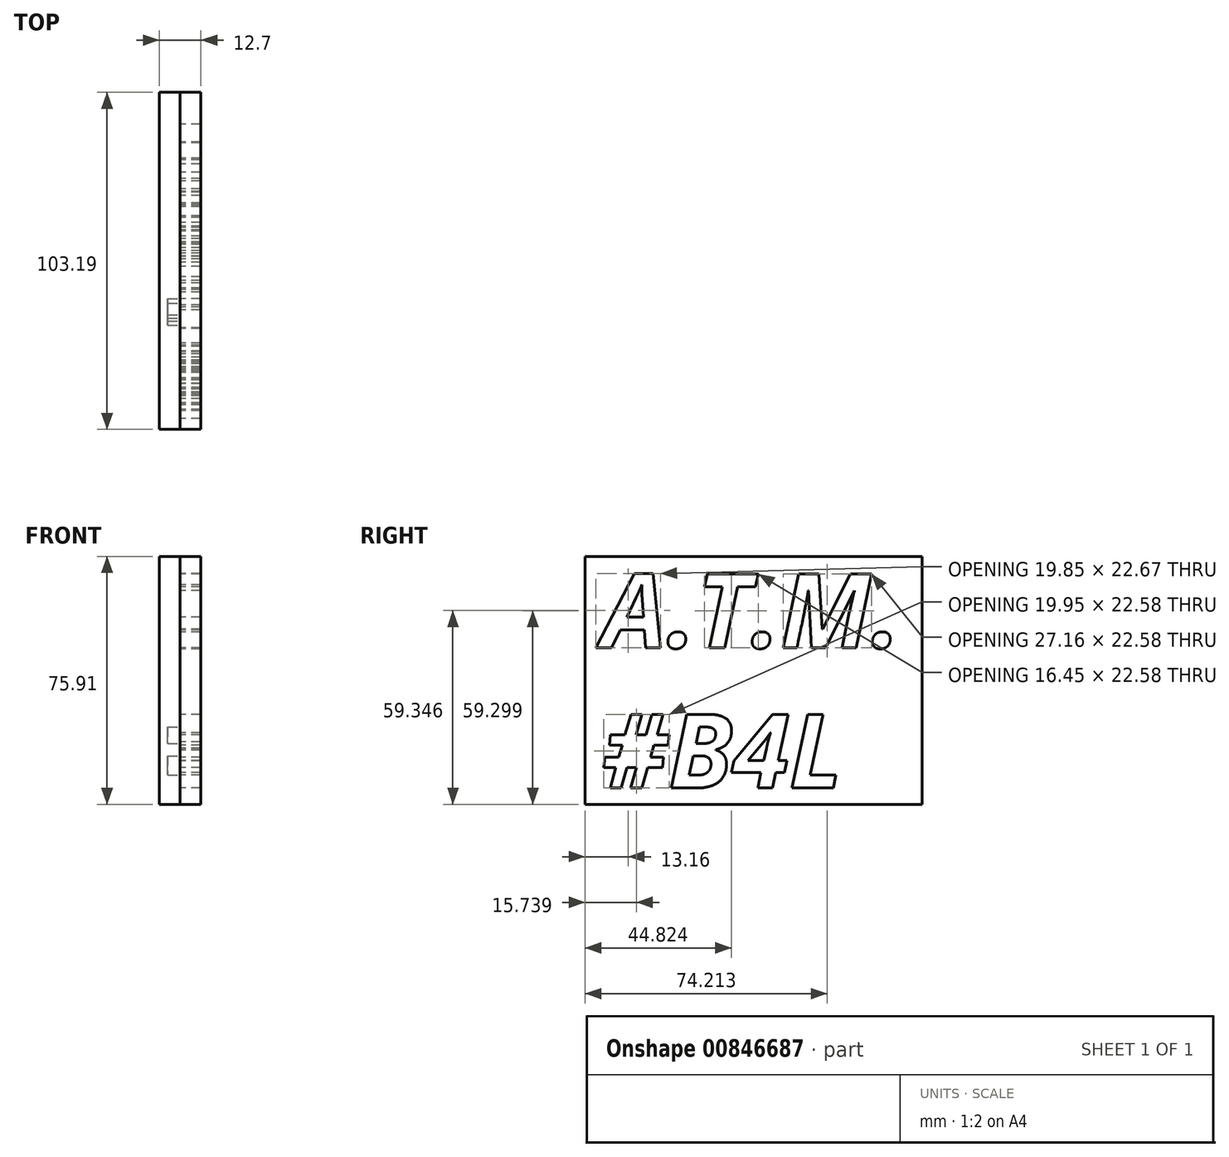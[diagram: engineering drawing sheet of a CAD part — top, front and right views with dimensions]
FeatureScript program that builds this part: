
annotation { "Feature Type Name" : "Feature", "Feature Type Description" : "" }
export const myFeature = defineFeature(function(context is Context, id is Id, definition is map)
    precondition{}
    {
        {
            var Q0;
            Q0=qCreatedBy(makeId("Right.planeOp"),FACE);
            var sketch = newSketch(context, id + "F0", { "sketchPlane" : qUnion([Q0])});
            skLineSegment(sketch, "E0.bottom", {"start": v(-51.7, 33.34) * mm, "end": v(51.5, 33.34) * mm});
            skLineSegment(sketch, "E0.top", {"start": v(-51.7, -42.57) * mm, "end": v(51.5, -42.57) * mm});
            skLineSegment(sketch, "E0.left", {"start": v(-51.7, 33.34) * mm, "end": v(-51.7, -42.57) * mm});
            skLineSegment(sketch, "E0.right", {"start": v(51.5, 33.34) * mm, "end": v(51.5, -42.57) * mm});
            skText(sketch, "E1", { "text": "A.T.M.\n#B4L\n", "fontName": "OpenSans-BoldItalic.ttf"});
            const initialGuessF0  = {"E1": [-0.04657, 0.00544, 1, 0, 0.02277]};
            skSetInitialGuess(sketch, initialGuessF0);
            skSolve(sketch);
        }
        {
            var Q0;
            Q0 = qSketchRegion(id + "F0", true);
            var Q1;
            Q1=makeQuery(id+"F0.imprint","IMPRINT",FACE,{"disambiguationData":[TD([[makeQuery(id+"F0.imprint","IMPRINT",EDGE,{"derivedFrom":sQuery(id+"F0.wireOp",EDGE,"E1.sketch_text.stroke-8")}),1.0]])]});
            var Q2;
            Q2=makeQuery(id+"F0.imprint","IMPRINT",FACE,{"disambiguationData":[TD([[makeQuery(id+"F0.imprint","IMPRINT",EDGE,{"derivedFrom":sQuery(id+"F0.wireOp",EDGE,"E1.sketch_text.stroke-131")}),1.0]])]});
            extrude(context, id + "F1", {"entities" : qUnion([Q0, Q1, Q2]), "depth" : 6.35 * mm, "offsetDistance" : 25.4 * mm});
        }
        {
            var Q0;
            Q0=makeQuery(id+"F0.imprint","IMPRINT",FACE,{"disambiguationData":[TD([[makeQuery(id+"F0.imprint","IMPRINT",EDGE,{"derivedFrom":sQuery(id+"F0.wireOp",EDGE,"E1.sketch_text.stroke-108")}),1.0]])]});
            var Q1;
            Q1=makeQuery(id+"F0.imprint","IMPRINT",FACE,{"disambiguationData":[TD([[makeQuery(id+"F0.imprint","IMPRINT",EDGE,{"derivedFrom":sQuery(id+"F0.wireOp",EDGE,"E1.sketch_text.stroke-114")}),1.0]])]});
            extrude(context, id + "F2", {"entities" : qUnion([Q0, Q1]), "operationType" : NewBodyOperationType.ADD, "oppositeDirection" : true, "depth" : 3.8 * mm, "offsetDistance" : 25.4 * mm});
        }
        {
            var Q0;
            Q0=makeQuery(id+"F1.opExtrude","CAP_FACE",FACE,{"disambiguationData":[OSD([sQuery(id+"F0.wireOp",EDGE,"E0.bottom"),sQuery(id+"F0.wireOp",EDGE,"E0.top"),sQuery(id+"F0.wireOp",EDGE,"E0.left"),sQuery(id+"F0.wireOp",EDGE,"E0.right"),sQuery(id+"F0.wireOp",EDGE,"E1.sketch_text.stroke-0"),sQuery(id+"F0.wireOp",EDGE,"E1.sketch_text.stroke-1"),sQuery(id+"F0.wireOp",EDGE,"E1.sketch_text.stroke-2"),sQuery(id+"F0.wireOp",EDGE,"E1.sketch_text.stroke-3"),sQuery(id+"F0.wireOp",EDGE,"E1.sketch_text.stroke-4"),sQuery(id+"F0.wireOp",EDGE,"E1.sketch_text.stroke-5"),sQuery(id+"F0.wireOp",EDGE,"E1.sketch_text.stroke-6"),sQuery(id+"F0.wireOp",EDGE,"E1.sketch_text.stroke-7"),sQuery(id+"F0.wireOp",EDGE,"E1.sketch_text.stroke-14"),sQuery(id+"F0.wireOp",EDGE,"E1.sketch_text.stroke-15"),sQuery(id+"F0.wireOp",EDGE,"E1.sketch_text.stroke-16"),sQuery(id+"F0.wireOp",EDGE,"E1.sketch_text.stroke-17"),sQuery(id+"F0.wireOp",EDGE,"E1.sketch_text.stroke-18"),sQuery(id+"F0.wireOp",EDGE,"E1.sketch_text.stroke-19"),sQuery(id+"F0.wireOp",EDGE,"E1.sketch_text.stroke-20"),sQuery(id+"F0.wireOp",EDGE,"E1.sketch_text.stroke-21"),sQuery(id+"F0.wireOp",EDGE,"E1.sketch_text.stroke-22"),sQuery(id+"F0.wireOp",EDGE,"E1.sketch_text.stroke-23"),sQuery(id+"F0.wireOp",EDGE,"E1.sketch_text.stroke-24"),sQuery(id+"F0.wireOp",EDGE,"E1.sketch_text.stroke-25"),sQuery(id+"F0.wireOp",EDGE,"E1.sketch_text.stroke-26"),sQuery(id+"F0.wireOp",EDGE,"E1.sketch_text.stroke-27"),sQuery(id+"F0.wireOp",EDGE,"E1.sketch_text.stroke-28"),sQuery(id+"F0.wireOp",EDGE,"E1.sketch_text.stroke-29"),sQuery(id+"F0.wireOp",EDGE,"E1.sketch_text.stroke-30"),sQuery(id+"F0.wireOp",EDGE,"E1.sketch_text.stroke-31"),sQuery(id+"F0.wireOp",EDGE,"E1.sketch_text.stroke-32"),sQuery(id+"F0.wireOp",EDGE,"E1.sketch_text.stroke-33"),sQuery(id+"F0.wireOp",EDGE,"E1.sketch_text.stroke-34"),sQuery(id+"F0.wireOp",EDGE,"E1.sketch_text.stroke-35"),sQuery(id+"F0.wireOp",EDGE,"E1.sketch_text.stroke-36"),sQuery(id+"F0.wireOp",EDGE,"E1.sketch_text.stroke-37"),sQuery(id+"F0.wireOp",EDGE,"E1.sketch_text.stroke-38"),sQuery(id+"F0.wireOp",EDGE,"E1.sketch_text.stroke-39"),sQuery(id+"F0.wireOp",EDGE,"E1.sketch_text.stroke-40"),sQuery(id+"F0.wireOp",EDGE,"E1.sketch_text.stroke-41"),sQuery(id+"F0.wireOp",EDGE,"E1.sketch_text.stroke-42"),sQuery(id+"F0.wireOp",EDGE,"E1.sketch_text.stroke-43"),sQuery(id+"F0.wireOp",EDGE,"E1.sketch_text.stroke-44"),sQuery(id+"F0.wireOp",EDGE,"E1.sketch_text.stroke-45"),sQuery(id+"F0.wireOp",EDGE,"E1.sketch_text.stroke-46"),sQuery(id+"F0.wireOp",EDGE,"E1.sketch_text.stroke-47"),sQuery(id+"F0.wireOp",EDGE,"E1.sketch_text.stroke-48"),sQuery(id+"F0.wireOp",EDGE,"E1.sketch_text.stroke-49"),sQuery(id+"F0.wireOp",EDGE,"E1.sketch_text.stroke-50"),sQuery(id+"F0.wireOp",EDGE,"E1.sketch_text.stroke-51"),sQuery(id+"F0.wireOp",EDGE,"E1.sketch_text.stroke-52"),sQuery(id+"F0.wireOp",EDGE,"E1.sketch_text.stroke-53"),sQuery(id+"F0.wireOp",EDGE,"E1.sketch_text.stroke-54"),sQuery(id+"F0.wireOp",EDGE,"E1.sketch_text.stroke-55"),sQuery(id+"F0.wireOp",EDGE,"E1.sketch_text.stroke-56"),sQuery(id+"F0.wireOp",EDGE,"E1.sketch_text.stroke-57"),sQuery(id+"F0.wireOp",EDGE,"E1.sketch_text.stroke-58"),sQuery(id+"F0.wireOp",EDGE,"E1.sketch_text.stroke-59"),sQuery(id+"F0.wireOp",EDGE,"E1.sketch_text.stroke-60"),sQuery(id+"F0.wireOp",EDGE,"E1.sketch_text.stroke-61"),sQuery(id+"F0.wireOp",EDGE,"E1.sketch_text.stroke-62"),sQuery(id+"F0.wireOp",EDGE,"E1.sketch_text.stroke-63"),sQuery(id+"F0.wireOp",EDGE,"E1.sketch_text.stroke-64"),sQuery(id+"F0.wireOp",EDGE,"E1.sketch_text.stroke-65"),sQuery(id+"F0.wireOp",EDGE,"E1.sketch_text.stroke-66"),sQuery(id+"F0.wireOp",EDGE,"E1.sketch_text.stroke-67"),sQuery(id+"F0.wireOp",EDGE,"E1.sketch_text.stroke-68"),sQuery(id+"F0.wireOp",EDGE,"E1.sketch_text.stroke-69"),sQuery(id+"F0.wireOp",EDGE,"E1.sketch_text.stroke-70"),sQuery(id+"F0.wireOp",EDGE,"E1.sketch_text.stroke-71"),sQuery(id+"F0.wireOp",EDGE,"E1.sketch_text.stroke-72"),sQuery(id+"F0.wireOp",EDGE,"E1.sketch_text.stroke-73"),sQuery(id+"F0.wireOp",EDGE,"E1.sketch_text.stroke-74"),sQuery(id+"F0.wireOp",EDGE,"E1.sketch_text.stroke-75"),sQuery(id+"F0.wireOp",EDGE,"E1.sketch_text.stroke-76"),sQuery(id+"F0.wireOp",EDGE,"E1.sketch_text.stroke-77"),sQuery(id+"F0.wireOp",EDGE,"E1.sketch_text.stroke-78"),sQuery(id+"F0.wireOp",EDGE,"E1.sketch_text.stroke-79"),sQuery(id+"F0.wireOp",EDGE,"E1.sketch_text.stroke-80"),sQuery(id+"F0.wireOp",EDGE,"E1.sketch_text.stroke-81"),sQuery(id+"F0.wireOp",EDGE,"E1.sketch_text.stroke-82"),sQuery(id+"F0.wireOp",EDGE,"E1.sketch_text.stroke-83"),sQuery(id+"F0.wireOp",EDGE,"E1.sketch_text.stroke-84"),sQuery(id+"F0.wireOp",EDGE,"E1.sketch_text.stroke-85"),sQuery(id+"F0.wireOp",EDGE,"E1.sketch_text.stroke-86"),sQuery(id+"F0.wireOp",EDGE,"E1.sketch_text.stroke-87"),sQuery(id+"F0.wireOp",EDGE,"E1.sketch_text.stroke-88"),sQuery(id+"F0.wireOp",EDGE,"E1.sketch_text.stroke-89"),sQuery(id+"F0.wireOp",EDGE,"E1.sketch_text.stroke-90"),sQuery(id+"F0.wireOp",EDGE,"E1.sketch_text.stroke-91"),sQuery(id+"F0.wireOp",EDGE,"E1.sketch_text.stroke-96"),sQuery(id+"F0.wireOp",EDGE,"E1.sketch_text.stroke-97"),sQuery(id+"F0.wireOp",EDGE,"E1.sketch_text.stroke-98"),sQuery(id+"F0.wireOp",EDGE,"E1.sketch_text.stroke-99"),sQuery(id+"F0.wireOp",EDGE,"E1.sketch_text.stroke-100"),sQuery(id+"F0.wireOp",EDGE,"E1.sketch_text.stroke-101"),sQuery(id+"F0.wireOp",EDGE,"E1.sketch_text.stroke-102"),sQuery(id+"F0.wireOp",EDGE,"E1.sketch_text.stroke-103"),sQuery(id+"F0.wireOp",EDGE,"E1.sketch_text.stroke-104"),sQuery(id+"F0.wireOp",EDGE,"E1.sketch_text.stroke-105"),sQuery(id+"F0.wireOp",EDGE,"E1.sketch_text.stroke-106"),sQuery(id+"F0.wireOp",EDGE,"E1.sketch_text.stroke-107"),sQuery(id+"F0.wireOp",EDGE,"E1.sketch_text.stroke-120"),sQuery(id+"F0.wireOp",EDGE,"E1.sketch_text.stroke-121"),sQuery(id+"F0.wireOp",EDGE,"E1.sketch_text.stroke-122"),sQuery(id+"F0.wireOp",EDGE,"E1.sketch_text.stroke-123"),sQuery(id+"F0.wireOp",EDGE,"E1.sketch_text.stroke-124"),sQuery(id+"F0.wireOp",EDGE,"E1.sketch_text.stroke-125"),sQuery(id+"F0.wireOp",EDGE,"E1.sketch_text.stroke-126"),sQuery(id+"F0.wireOp",EDGE,"E1.sketch_text.stroke-127"),sQuery(id+"F0.wireOp",EDGE,"E1.sketch_text.stroke-128"),sQuery(id+"F0.wireOp",EDGE,"E1.sketch_text.stroke-129"),sQuery(id+"F0.wireOp",EDGE,"E1.sketch_text.stroke-130"),sQuery(id+"F0.wireOp",EDGE,"E1.sketch_text.stroke-138"),sQuery(id+"F0.wireOp",EDGE,"E1.sketch_text.stroke-139"),sQuery(id+"F0.wireOp",EDGE,"E1.sketch_text.stroke-140"),sQuery(id+"F0.wireOp",EDGE,"E1.sketch_text.stroke-141"),sQuery(id+"F0.wireOp",EDGE,"E1.sketch_text.stroke-142"),sQuery(id+"F0.wireOp",EDGE,"E1.sketch_text.stroke-143")])],"isStart":true});
            var sketch = newSketch(context, id + "F3", { "sketchPlane" : qUnion([Q0])});
            skLineSegment(sketch, "E2", {"start": v(-51.5, -42.57) * mm, "end": v(-51.5, 33.34) * mm});
            skLineSegment(sketch, "E3", {"start": v(-51.5, 33.34) * mm, "end": v(51.7, 33.34) * mm});
            skLineSegment(sketch, "E4", {"start": v(51.7, 33.34) * mm, "end": v(51.7, -42.57) * mm});
            skLineSegment(sketch, "E5", {"start": v(51.7, -42.57) * mm, "end": v(-51.5, -42.57) * mm});
            skSolve(sketch);
        }
        {
            var Q0;
            Q0 = qSketchRegion(id + "F3", true);
            extrude(context, id + "F4", {"entities" : qUnion([Q0]), "depth" : 6.35 * mm, "offsetDistance" : 25.4 * mm});
        }
    });
